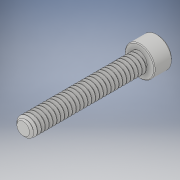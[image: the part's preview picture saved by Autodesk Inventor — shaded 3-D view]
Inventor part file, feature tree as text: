
AUTODESK INVENTOR PART (.ipt)
format: ipt  version: 2018 (Build 220112000, 112)  size: 1,001,984 bytes
history: native  units: in
note: dims shown in document units (in); Inventor stores cm internally (conversion verified against a paired STEP export)
features: chamfer x1
ambient origin geometry x8: Origin, YZ Plane, XZ Plane, XY Plane, X Axis, Y Axis, Z Axis, Center Point
bodies: Solid1 (feature_tree)
feature tree (1):
  chamfer  "Chamfer2"  [1 undecoded]
note: 1 required parameter value undecoded (feature->parameter linkage not recoverable at this tier; creation-order binding heuristic only, values carry confidence <= 0.55)
